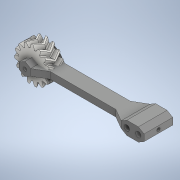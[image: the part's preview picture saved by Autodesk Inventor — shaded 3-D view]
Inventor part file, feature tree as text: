
AUTODESK INVENTOR PART (.ipt)
format: ipt  version: 2020 (Build 240168000, 168)  size: 986,112 bytes
history: native  units: in
note: dims shown in document units (in); Inventor stores cm internally (conversion verified against a paired STEP export)
features: sketch x5, extrude x4, other x3, plane x2, mirror x1, projected_geometry x1
ambient origin geometry x8: Origin, YZ Plane, XZ Plane, XY Plane, X Axis, Y Axis, Z Axis, Center Point
bodies: Solid1 (feature_tree), Solid2 (feature_tree)
feature tree (16):
  other  "Spur Gear1"
  plane  "Work Plane3"
  extrude  "Extrusion1"  Depth=3.4256in
  plane  "Work Plane1"
  extrude  "Extrusion2"  Depth=0.7874in
  sketch  "Sketch4"  dims[d4=0.0in d5=0.0906in]
  extrude  "Extrusion4"  Depth=0.0906in
  mirror  "Mirror3"
  extrude  "Extrusion11"  Depth=0.315in
  sketch  "Sketch1"  dims[d0=0.1818in d1=3.4256in]
  sketch  "Sketch2"  dims[d2=0.0945in d3=0.7874in]
  sketch  "Sketch5"  dims[d6=0.7874in d7=0.0in d29=0.315in]
  other  "Solid1::Spur Gear1"
  other  "TaggingFeature1"
  projected_geometry  "Projected Loop11"
  sketch  "Sketch15"  dims[d31=0.315in d33=0.1476in d34=0.2362in d35=0.0in d38=0.315in d69=2.4807in d70=0.3937in d71=0.1969in d79=0.0in d80=0.3937in d81=0.0in]
